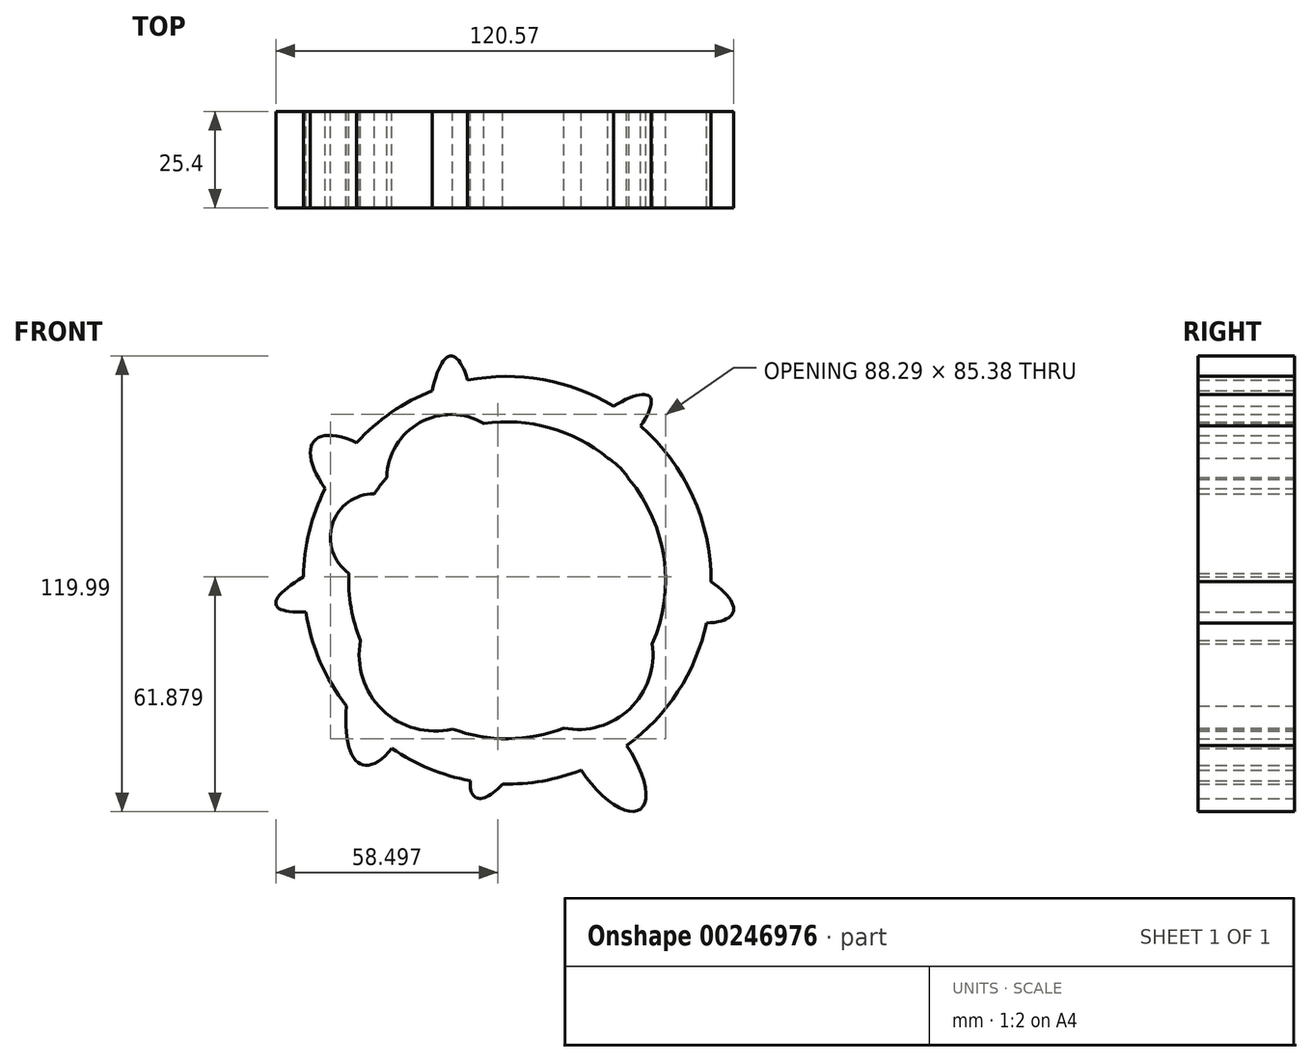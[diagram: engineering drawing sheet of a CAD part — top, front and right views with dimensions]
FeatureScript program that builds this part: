
annotation { "Feature Type Name" : "Feature", "Feature Type Description" : "" }
export const myFeature = defineFeature(function(context is Context, id is Id, definition is map)
    precondition{}
    {
        {
            var Q0;
            Q0=qCreatedBy(makeId("Front.planeOp"),FACE);
            var sketch = newSketch(context, id + "F0", { "sketchPlane" : qUnion([Q0])});
            skCircle(sketch, "E0", {"center": v(0, 0) * mm, "radius": 9.36 * mm});
            skCircle(sketch, "E1", {"center": v(0, 0) * mm, "radius": 25.77 * mm});
            skCircle(sketch, "E2", {"center": v(0, 0) * mm, "radius": 41.72 * mm});
            skCircle(sketch, "E3", {"center": v(0, 0) * mm, "radius": 53.7 * mm});
            skCircle(sketch, "E4", {"center": v(18.71, -19.6) * mm, "radius": 19.7 * mm});
            skPoint(sketch, "E4.first.point", {"position": v(16.65, 0) * mm});
            skPoint(sketch, "E4.second.point", {"position": v(0, -25.77) * mm});
            skPoint(sketch, "E4.third.point", {"position": v(38.21, -16.75) * mm});
            skCircle(sketch, "E5", {"center": v(-19.02, -19.76) * mm, "radius": 19.94 * mm});
            skPoint(sketch, "E5.first.point", {"position": v(-16.35, 0) * mm});
            skPoint(sketch, "E5.third.point", {"position": v(-28.29, -37.42) * mm});
            skCircle(sketch, "E6", {"center": v(17.38, 17.39) * mm, "radius": 17.4 * mm});
            skPoint(sketch, "E6.second.point", {"position": v(0, 18.27) * mm});
            skPoint(sketch, "E6.third.point", {"position": v(32.16, 26.57) * mm});
            skCircle(sketch, "E7", {"center": v(-14.79, 26.75) * mm, "radius": 16.9 * mm});
            skPoint(sketch, "E7.first.point", {"position": v(-13.85, 9.87) * mm});
            skPoint(sketch, "E7.second.point", {"position": v(-31.7, 27.14) * mm});
            skPoint(sketch, "E7.third.point", {"position": v(2.09, 25.7) * mm});
            skCircle(sketch, "E8", {"center": v(-35.05, 11.28) * mm, "radius": 11.52 * mm});
            skPoint(sketch, "E8.first.point", {"position": v(-25.23, 5.25) * mm});
            skPoint(sketch, "E8.second.point", {"position": v(-43.17, 19.45) * mm});
            skPoint(sketch, "E8.third.point", {"position": v(-32.7, 0) * mm});
            skEllipse(sketch, "E9", {"center": v(0, -41.72) * mm, "majorRadius": 17.56 * mm, "minorRadius": 5.89 * mm, "majorAxis": v(0.47, 0.88)});
            skEllipse(sketch, "E10", {"center": v(25.75, -47.12) * mm, "majorRadius": 16.14 * mm, "minorRadius": 6.78 * mm, "majorAxis": v(-0.57, 0.82)});
            skEllipse(sketch, "E11", {"center": v(34.77, 0) * mm, "majorRadius": 26.14 * mm, "minorRadius": 7.95 * mm, "majorAxis": v(0.95, -0.32)});
            skEllipse(sketch, "E12", {"center": v(-29.61, -20.48) * mm, "majorRadius": 29.4 * mm, "minorRadius": 10.01 * mm, "majorAxis": v(-0.3, -0.96)});
            skEllipse(sketch, "E13", {"center": v(22.64, 35.05) * mm, "majorRadius": 19.98 * mm, "minorRadius": 5.43 * mm, "majorAxis": v(0.75, 0.66)});
            skEllipse(sketch, "E14", {"center": v(-14.73, 32.41) * mm, "majorRadius": 26.67 * mm, "minorRadius": 6.65 * mm, "majorAxis": v(0, 1)});
            skEllipse(sketch, "E15", {"center": v(-34.94, 22.8) * mm, "majorRadius": 21.1 * mm, "minorRadius": 8.73 * mm, "majorAxis": v(-0.75, 0.66)});
            skEllipse(sketch, "E16", {"center": v(-25.23, 5.25) * mm, "majorRadius": 37.5 * mm, "minorRadius": 7.28 * mm, "majorAxis": v(-0.95, -0.31)});
            skSolve(sketch);
        }
        {
            var Q0;
            Q0 = qSketchRegion(id + "F0", true);
            extrude(context, id + "F1", {"entities" : qUnion([Q0]), "depth" : 25.4 * mm});
        }
    });
